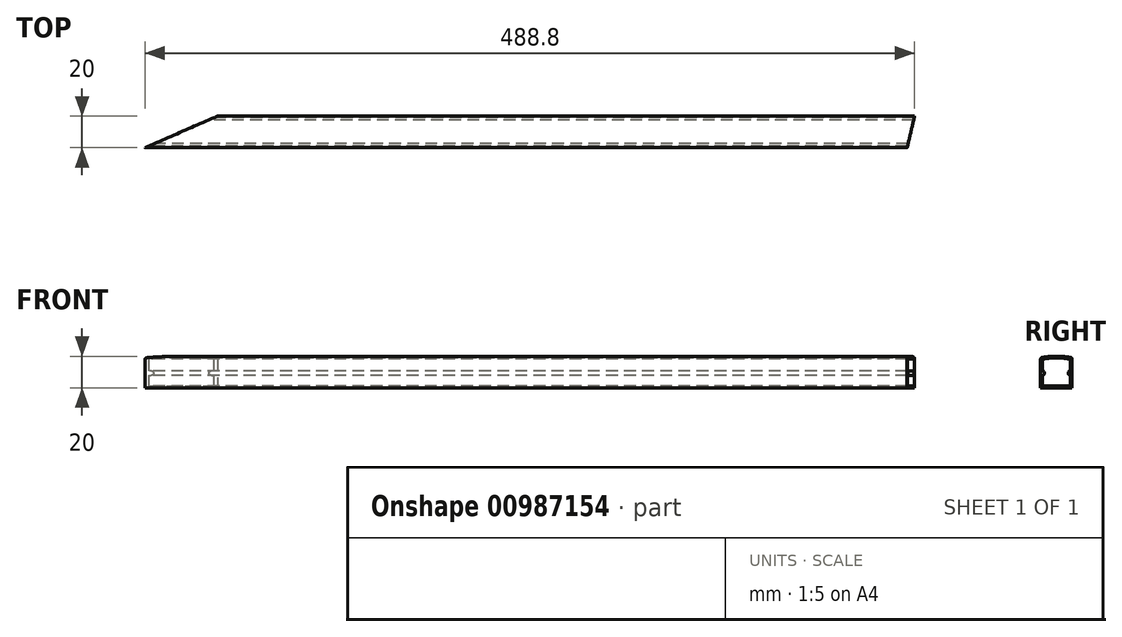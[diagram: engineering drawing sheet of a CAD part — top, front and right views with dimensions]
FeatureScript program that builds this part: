
annotation { "Feature Type Name" : "Feature", "Feature Type Description" : "" }
export const myFeature = defineFeature(function(context is Context, id is Id, definition is map)
    precondition{}
    {
        {
            var Q0;
            Q0=qCreatedBy(makeId("Right.planeOp"),FACE);
            var sketch = newSketch(context, id + "F0", { "sketchPlane" : qUnion([Q0])});
            skLineSegment(sketch, "E0.bottom", {"start": v(-10, -10) * mm, "end": v(10, -10) * mm});
            skLineSegment(sketch, "E0.top", {"start": v(-10, 10) * mm, "end": v(10, 10) * mm});
            skLineSegment(sketch, "E0.left", {"start": v(-10, -10) * mm, "end": v(-10, 10) * mm});
            skLineSegment(sketch, "E0.right", {"start": v(10, -10) * mm, "end": v(10, 10) * mm});
            skPoint(sketch, "E0.middle", {"position": v(0, 0) * mm});
            skSolve(sketch);
        }
        {
            var Q0;
            Q0=qCreatedBy(makeId("Right.planeOp"),FACE);
            var sketch = newSketch(context, id + "F1", { "sketchPlane" : qUnion([Q0])});
            skLineSegment(sketch, "E1.0", {"start": v(0, -10) * mm, "end": v(10, -10) * mm});
            skLineSegment(sketch, "E1.3", {"start": v(10, -10) * mm, "end": v(10, -0.2) * mm});
            skPoint(sketch, "E1.4", {"position": v(0, 0) * mm});
            skLineSegment(sketch, "E2.0", {"start": v(9, -9) * mm, "end": v(9, -2.2) * mm});
            skLineSegment(sketch, "E2.1", {"start": v(0, -9) * mm, "end": v(9, -9) * mm});
            skLineSegment(sketch, "E3", {"start": v(10, -0.2) * mm, "end": v(9, -0.2) * mm});
            skArc(sketch, "E4", {"start": v(9, -0.2) * mm, "mid": v(8.5, -0.7) * mm, "end": v(9, -1.2) * mm});
            skArc(sketch, "E5", {"start": v(9, -2.2) * mm, "mid": v(9.5, -1.7) * mm, "end": v(9, -1.2) * mm});
            skLineSegment(sketch, "E6", {"start": v(0, -9) * mm, "end": v(0, -10) * mm});
            skPoint(sketch, "E1.1.end.orphan", {"position": v(10, 10) * mm});
            skPoint(sketch, "E1.1.start.orphan", {"position": v(-10, 10) * mm});
            skPoint(sketch, "E1.2.end.orphan", {"position": v(-10, 10) * mm});
            skPoint(sketch, "E1.2.start.orphan", {"position": v(-10, -10) * mm});
            skPoint(sketch, "E7.orphan", {"position": v(-9, -9) * mm});
            skSolve(sketch);
        }
        {
            var Q0;
            Q0=qSketchRegion(id+"F1",true);
            extrude(context, id + "F2", {"entities" : qUnion([Q0]), "depth" : 1000 * mm, "offsetDistance" : 25 * mm});
        }
        {
            var Q0;
            Q0=qCreatedBy(makeId("Right.planeOp"),FACE);
            var sketch = newSketch(context, id + "F3", { "sketchPlane" : qUnion([Q0])});
            skPoint(sketch, "E8.2", {"position": v(0, 0) * mm});
            skLineSegment(sketch, "E8.5", {"start": v(10, -0.2) * mm, "end": v(9, -0.2) * mm});
            skArc(sketch, "E8.6", {"start": v(9, -0.2) * mm, "mid": v(8.5, -0.7) * mm, "end": v(9, -1.2) * mm});
            skArc(sketch, "E8.7", {"start": v(9, -2.2) * mm, "mid": v(9.5, -1.7) * mm, "end": v(9, -1.2) * mm});
            skPoint(sketch, "E8.9", {"position": v(10, 10) * mm});
            skPoint(sketch, "E8.10", {"position": v(10, 10) * mm});
            skPoint(sketch, "E8.11", {"position": v(-10, 10) * mm});
            skPoint(sketch, "E8.12", {"position": v(-10, 10) * mm});
            skPoint(sketch, "E8.13", {"position": v(-10, -10) * mm});
            skPoint(sketch, "E8.14", {"position": v(-9, -9) * mm});
            skPoint(sketch, "E8.15", {"position": v(-10, -10) * mm});
            skPoint(sketch, "E8.1.end.orphan", {"position": v(10, -0.2) * mm});
            skPoint(sketch, "E8.1.start.orphan", {"position": v(10, -10) * mm});
            skPoint(sketch, "E8.3.end.orphan", {"position": v(9, -2.2) * mm});
            skPoint(sketch, "E8.3.start.orphan", {"position": v(9, -9) * mm});
            skPoint(sketch, "E8.4.end.orphan", {"position": v(9, -9) * mm});
            skPoint(sketch, "E8.4.start.orphan", {"position": v(0, -9) * mm});
            skPoint(sketch, "E8.0.end.orphan", {"position": v(10, -10) * mm});
            skPoint(sketch, "E8.0.start.orphan", {"position": v(0, -10) * mm});
            skPoint(sketch, "E8.8.end.orphan", {"position": v(0, -10) * mm});
            skPoint(sketch, "E8.8.start.orphan", {"position": v(0, -9) * mm});
            skLineSegment(sketch, "E9", {"start": v(10, -0.2) * mm, "end": v(10, 8.17) * mm});
            skArc(sketch, "E10", {"start": v(9.18, 9.15) * mm, "mid": v(4.61, 9.79) * mm, "end": v(0, 10) * mm});
            skLineSegment(sketch, "E11", {"start": v(0, 10) * mm, "end": v(-15.57, 10) * mm, "construction": true});
            skPoint(sketch, "E12.visualSharp", {"position": v(10, 8.99) * mm});
            skArc(sketch, "E12.filletArc", {"start": v(10, 8.17) * mm, "mid": v(9.77, 8.8) * mm, "end": v(9.18, 9.15) * mm});
            skArc(sketch, "E13.0", {"start": v(9, 8.17) * mm, "mid": v(4.52, 8.8) * mm, "end": v(0, 9) * mm});
            skLineSegment(sketch, "E13.1", {"start": v(9, 0.8) * mm, "end": v(9, 8.17) * mm});
            skArc(sketch, "E13.2", {"start": v(9, 0.8) * mm, "mid": v(7.5, -0.7) * mm, "end": v(9, -2.2) * mm});
            skLineSegment(sketch, "E14", {"start": v(0, 10) * mm, "end": v(0, 9) * mm});
            skSolve(sketch);
        }
        {
            var Q0;
            Q0=qSketchRegion(id+"F3",true);
            extrude(context, id + "F4", {"entities" : qUnion([Q0]), "depth" : 1000 * mm, "offsetDistance" : 25 * mm});
        }
        {
            var Q0;
            Q0=makeQuery(id+"F2.opExtrude","SWEPT_BODY",BODY,{"disambiguationData":[OSD([sQuery(id+"F1.wireOp",EDGE,"E1.0"),sQuery(id+"F1.wireOp",EDGE,"E1.3"),sQuery(id+"F1.wireOp",EDGE,"E2.0"),sQuery(id+"F1.wireOp",EDGE,"E2.1"),sQuery(id+"F1.wireOp",EDGE,"E3"),sQuery(id+"F1.wireOp",EDGE,"E4"),sQuery(id+"F1.wireOp",EDGE,"E5"),sQuery(id+"F1.wireOp",EDGE,"E6")])]});
            var Q1;
            Q1=qCreatedBy(makeId("Front.planeOp"),FACE);
            mirror(context, id + "F5", {"operationType" : NewBodyOperationType.ADD, "entities" : qUnion([Q0]), "mirrorPlane" : qUnion([Q1])});
        }
        {
            var Q0;
            Q0=makeQuery(id+"F4.opExtrude","SWEPT_BODY",BODY,{"disambiguationData":[OSD([sQuery(id+"F3.wireOp",EDGE,"E8.5"),sQuery(id+"F3.wireOp",EDGE,"E8.6"),sQuery(id+"F3.wireOp",EDGE,"E8.7"),sQuery(id+"F3.wireOp",EDGE,"E9"),sQuery(id+"F3.wireOp",EDGE,"E10"),sQuery(id+"F3.wireOp",EDGE,"E12.filletArc"),sQuery(id+"F3.wireOp",EDGE,"E13.0"),sQuery(id+"F3.wireOp",EDGE,"E13.1"),sQuery(id+"F3.wireOp",EDGE,"E13.2"),sQuery(id+"F3.wireOp",EDGE,"E14")])]});
            var Q1;
            Q1=qCreatedBy(makeId("Front.planeOp"),FACE);
            mirror(context, id + "F6", {"operationType" : NewBodyOperationType.ADD, "entities" : qUnion([Q0]), "mirrorPlane" : qUnion([Q1])});
        }
        {
            var Q0;
            Q0=qCreatedBy(makeId("Top.planeOp"),FACE);
            var sketch = newSketch(context, id + "F7", { "sketchPlane" : qUnion([Q0])});
            skLineSegment(sketch, "E15", {"start": v(0, 0) * mm, "end": v(0, -10) * mm});
            skLineSegment(sketch, "E16", {"start": v(0, 10) * mm, "end": v(0, 0) * mm});
            skLineSegment(sketch, "E17", {"start": v(488.8, 10) * mm, "end": v(709.91, 10) * mm});
            skLineSegment(sketch, "E18.bottom", {"start": v(484, -10) * mm, "end": v(1016.96, -10) * mm});
            skLineSegment(sketch, "E18.top", {"start": v(488.8, 10) * mm, "end": v(1016.96, 10) * mm});
            skLineSegment(sketch, "E18.right", {"start": v(1016.96, -10) * mm, "end": v(1016.96, 10) * mm});
            skLineSegment(sketch, "E19", {"start": v(484, 10) * mm, "end": v(484, -10) * mm, "construction": true});
            skLineSegment(sketch, "E20", {"start": v(0, 10) * mm, "end": v(46, 10) * mm});
            skLineSegment(sketch, "E21", {"start": v(46, 10) * mm, "end": v(0, -10) * mm});
            skPoint(sketch, "E22.end.orphan", {"position": v(6.04, -10) * mm});
            skLineSegment(sketch, "E23", {"start": v(484, -10) * mm, "end": v(488.8, 10) * mm});
            skSolve(sketch);
        }
        {
            var Q0;
            Q0=qSketchRegion(id+"F7",true);
            extrude(context, id + "F8", {"entities" : qUnion([Q0]), "operationType" : NewBodyOperationType.REMOVE, "endBound" : BoundingType.THROUGH_ALL, "depth" : 25 * mm, "offsetDistance" : 25 * mm, "hasSecondDirection" : true, "secondDirectionBound" : SecondDirectionBoundingType.THROUGH_ALL, "secondDirectionOppositeDirection" : true, "secondDirectionDepth" : 25 * mm});
        }
    });
